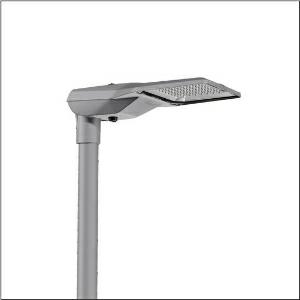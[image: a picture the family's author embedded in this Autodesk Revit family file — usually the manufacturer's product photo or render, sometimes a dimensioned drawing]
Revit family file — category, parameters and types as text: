
# Revit family: streetlight_sl_21_midi___p0_8a_5xe3u33t08mb_d2fa
name_source: partatom
category: Lighting Fixtures
units: mm (PartAtom-declared; Revit-internal decimal feet)

## family parameters
Cut with Voids When Loaded = No
Host = Face
Light Source = No
Part Type = Normal
Room Calculation Point = No
Round Connector Dimension = Use Diameter
Shared = No

## types (1)
- --- (1 x LED, 18430 lm, 136 W, 3000K)
    Apparent Load = 136 VA
    CIE Flux Codes = 33 69 96 100 100
    Color Rendering = 70
    Color Temperature = 3000K
    Default Elevation = 1800 mm
    Description = Streetlight SL 21 midi, mast luminaire, primary light control with lens, of PMMA, primary optical cover: cover, of toughened safety glass, transparent, light distribution: P0.8a, light emission: direct distribution, primary light characteristic: asymmetric, installation type: post-top, side-entry, LED, High Power LED, rated luminous flux: 18.430lm, luminous efficacy: 136lm/W, light colour: 730, colour temperature: 3000K, control gear: D4i, control: pre-setting: logarithmic dimming characteristic, flexible luminous flux parameterisation, time-dependent luminous flux control, constant luminous flux control, overheat protection, mains connection: 230..240V, AC, 50/60Hz, start of lifetime: 136W, end of service life: 142W, reduction: 61W, luminaire housing, of diecast aluminium, powder-coated, Siteco® metallic grey (DB 702S), corrosivity category C5 mid according to DIN EN ISO 12944, multi-level sealing system, sealing non-destructively replaceable, inclination adjustable: 0°, 5°, 10°, 15°, please order mast flange separately, length: 644mm, width: 335mm, height: 110mm, mast flange for spigot size: 42mm (side-entry): 5XC10008XM4, 60/48mm (side-entry/post-top): 5XC10108XM2, 76/60mm (side-entry/post-top): 5XC10108XM1, mounting height: 4..8m, Smart Interface below and above, protection rating (complete): IP66, insulation class (complete): insulation class II (safety insulation), certification: CE, ENEC, ENEC+, VDE, impact resistance: IK10, permissible operating ambient temperature for outdoor applications: -40..+50°C, standard-compliant lighting for roads and squares, packaging unit: 1 piece

Light Distribution: P0.8a
    Height = 111 mm
    Lamp = 1 x LED
    Lamp Light Flux = 18430 lm
    Lamp Power = 136 W
    Lamp count = 1
    Length = 644 mm
    Luminous efficacy = 136 lm/W
    Manufacturer = Siteco
    ModVariant = No
    Model = 5XE3U33T08MB
    Number of Poles = 1
    OnlyDefault = Yes
    Power Factor = 1
    Product Name = Streetlight SL 21 midi | P0.8a
    Product group = mast luminaire | pylon top
    ProductGroupID = 6100
    Protection Class = Protection class II
    Protection Degree = IP 66
    RLX_Detail_Level = 1
    RLX_Emergency_Light_Flux = 0 lm
    RLX_Emergency_Type = 0
    RLX_Emergency_Type_DB = No
    RlxData = <blob elided: 91105 chars, md5=83b95c34>
    Socket = socket
    Standby Power = 0 W
    System Light Flux = 18429 lm
    System Power = 136 W
    Type Comments = factory setting: luminous flux: 100 % | dim-lin: 254 | 695 mA
    Type Image = l_1004304.jpg
    URL = http://relux.com
    VarID = @adj_094109
    Voltage = 0 V
    Weight = 0.00 kg
    Width = 336 mm

## geometry (parser evidence)
native form markers: Blend x4, Sweep x11
no freeform markers — native parametric forms only
